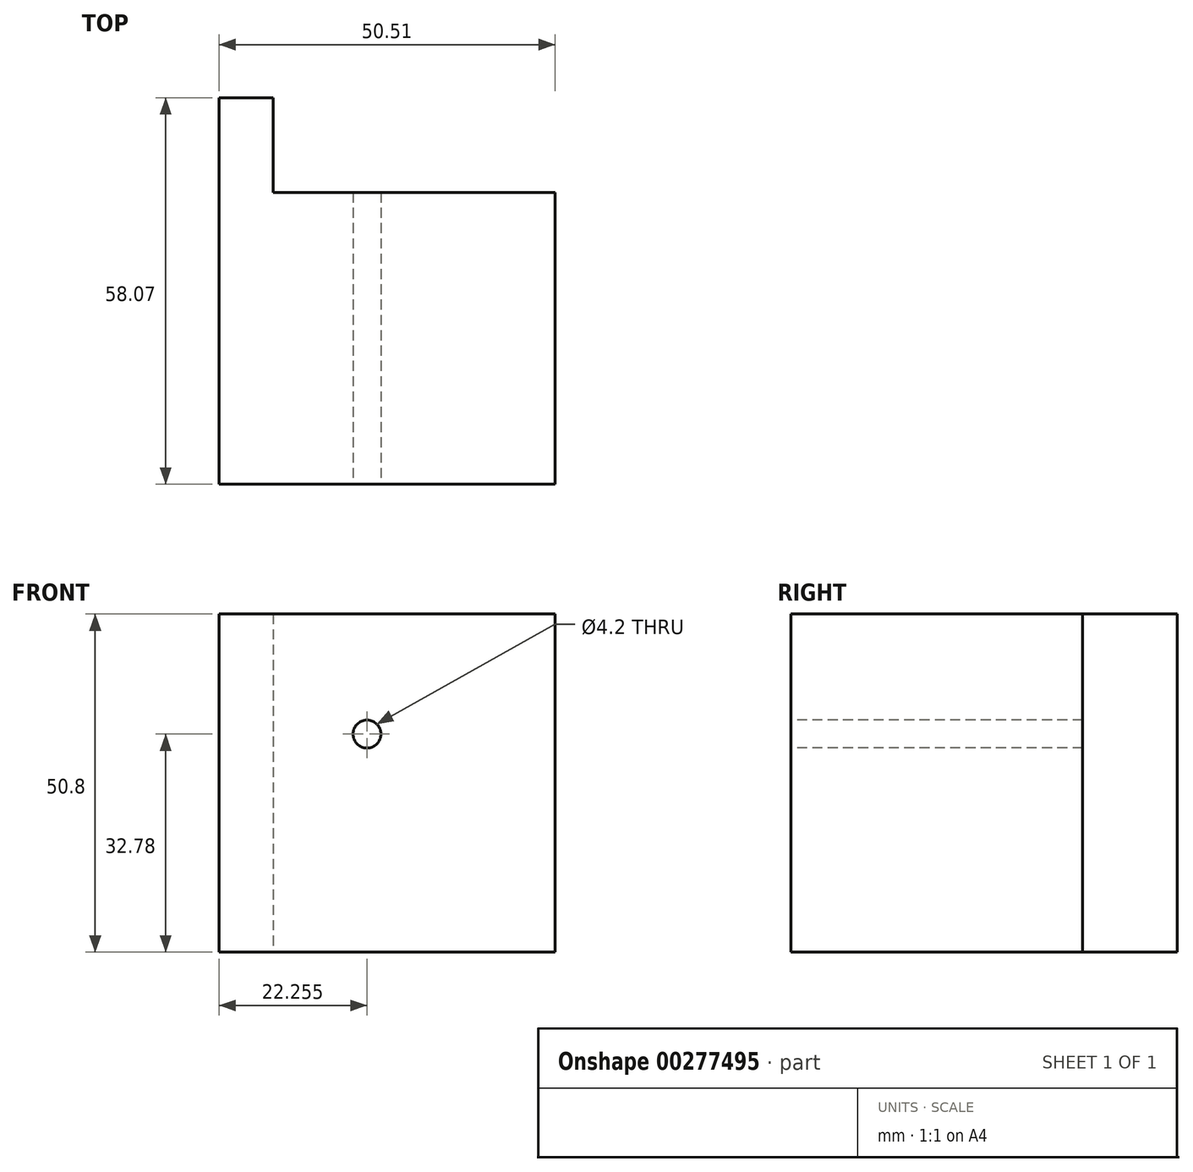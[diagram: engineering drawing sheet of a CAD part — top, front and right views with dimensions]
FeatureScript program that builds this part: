
annotation { "Feature Type Name" : "Feature", "Feature Type Description" : "" }
export const myFeature = defineFeature(function(context is Context, id is Id, definition is map)
    precondition{}
    {
        {
            var Q0;
            Q0=qCreatedBy(makeId("Top.planeOp"),FACE);
            var sketch = newSketch(context, id + "F0", { "sketchPlane" : qUnion([Q0])});
            skLineSegment(sketch, "E0", {"start": v(-116.25, 14.23) * mm, "end": v(-116.25, -43.84) * mm});
            skLineSegment(sketch, "E1", {"start": v(-116.25, -43.84) * mm, "end": v(-65.74, -43.84) * mm});
            skLineSegment(sketch, "E2", {"start": v(-65.74, -43.84) * mm, "end": v(-65.74, 0) * mm});
            skLineSegment(sketch, "E3", {"start": v(-65.74, 0) * mm, "end": v(-108.1, 0) * mm});
            skLineSegment(sketch, "E4", {"start": v(-108.1, 0) * mm, "end": v(-108.1, 14.23) * mm});
            skLineSegment(sketch, "E5", {"start": v(-108.1, 14.23) * mm, "end": v(-116.25, 14.23) * mm});
            skSolve(sketch);
        }
        {
            var Q0;
            Q0 = qSketchRegion(id + "F0", true);
            extrude(context, id + "F1", {"entities" : qUnion([Q0]), "depth" : 50.8 * mm});
        }
        {
            var Q0;
            Q0=makeQuery(id+"F1.opExtrude","SWEPT_FACE",FACE,{"disambiguationData":[OSD([sQuery(id+"F0.wireOp",EDGE,"E1")])]});
            var sketch = newSketch(context, id + "F2", { "sketchPlane" : qUnion([Q0])});
            skCircle(sketch, "E6", {"center": v(-94, 32.78) * mm, "radius": 9.96 * mm});
            skSolve(sketch);
        }
        {
            var Q0;
            Q0=sQuery(id+"F2.wireOp",VERTEX,"E6.center");
            var Q1;
            Q1=makeQuery(id+"F1.opExtrude","SWEPT_BODY",BODY,{"disambiguationData":[OSD([sQuery(id+"F0.wireOp",EDGE,"E0"),sQuery(id+"F0.wireOp",EDGE,"E1"),sQuery(id+"F0.wireOp",EDGE,"E2"),sQuery(id+"F0.wireOp",EDGE,"E3"),sQuery(id+"F0.wireOp",EDGE,"E4"),sQuery(id+"F0.wireOp",EDGE,"E5")])]});
            hole(context, id + "F3", {"style" : HoleStyle.SIMPLE, "endStyle" : HoleEndStyle.THROUGH, "standardTappedOrClearance" : lookupTablePath({ "standard" : "ISO", "engagement" : "75%", "pitch" : "0.8 mm", "size" : "M5", "type" : "Tapped" }), "standardBlindInLast" : lookupTablePath({ "standard" : "ISO", "engagement" : "75%", "pitch" : "0.8 mm", "size" : "M5", "type" : "Tapped" }), "holeDiameter" : 4.2 * mm, "showTappedDepth" : true, "tappedDepth" : 12.7 * mm, "tapClearance" : 3, "locations" : qUnion([Q0]), "scope" : qUnion([Q1]), "majorDiameter" : 5 * mm});
        }
    });
